# Revit family: FU_Seat_LAPSE 0310BC
name_source: partatom
category: Furniture
units: mm (PartAtom-declared; Revit-internal decimal feet)

## family parameters
Always vertical = Yes
Cut with Voids When Loaded = No
OmniClass Number = 23.40.20.00
OmniClass Title = General Furniture and Specialties
Render Appearance Source = Family Geometry
Room Calculation Point = No
Shared = No
Work Plane-Based = No

## types (1)
- LAP0310BC
    Default Elevation = 0 mm  [stored 0 ft]
    Depth = 350 mm  [stored 1.14829 ft]
    Description = Upholstered intermediate arm for the Lapse modular seating range.
    Elevation = 455 mm
    Height = 140 mm  [stored 0.459318 ft]
    Manufacturer = Sandler
    Model = LAP0310BC
    URL = https://www.sandlerseating.com
    Width = 140 mm  [stored 0.459318 ft]

note: [stored X ft] marks values corroborated as IEEE doubles in the binary element streams (Revit-internal decimal feet)

## geometry (parser evidence)
native form markers: Sweep x3
no freeform markers — native parametric forms only
